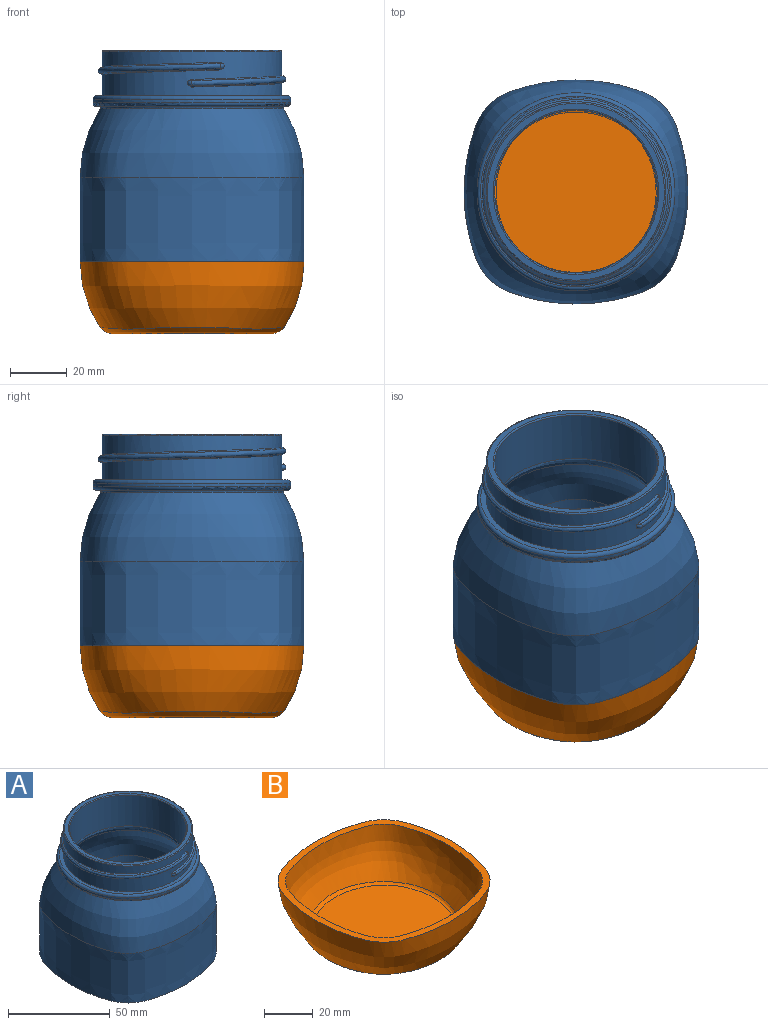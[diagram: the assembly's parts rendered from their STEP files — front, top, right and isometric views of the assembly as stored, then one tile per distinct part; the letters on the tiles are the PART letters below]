
ASSEMBLY  parts=2 mates=1
PART A: 27 faces, bbox 85.2x85.2x80.7 mm
  f0: cylinder r=31.75mm len=63.5mm, axis (0,0,-1), area 2519.4mm2, adj f1,f2,f5,f15,f19,f20,f22,f23
  f1: cone r=0.25mm half-angle=61.8deg, axis (-0.03,0,1), area 0.7mm2, adj f0,f19,f20
  f2: cone r=1.04mm half-angle=61.8deg, axis (0.03,0,-1), area 0.7mm2, adj f0,f19,f22
  f3: extruded ~78.99x78.99mm, area 7756.7mm2, adj f4,f26
  f4: bspline ~78.96x78.96mm, area 6303.1mm2, adj f3,f9
  f5: plane 67.31x67.31mm, normal (0,0,1), area 391.4mm2, adj f0,f18
  f6: plane 67.31x67.31mm, normal (0,0,-1), area 182.5mm2, adj f9,f17
  f7: cylinder r=34.92mm len=69.85mm, axis (0,0,-1), area 278.7mm2, adj f17,f18
  f8: plane 62.48x62.48mm, normal (0,0,1), area 385.9mm2, adj f15,f16
  f9: bspline ~65.42x65.42mm, area 228.7mm2, adj f4,f6
  f10: bspline ~59.42x59.41mm, area 630mm2, adj f12,f13
  f11: offset ~85.06x85.04mm, area 7156.8mm2, adj f12,f26
  f12: offset ~85.06x85.05mm, area 5387.2mm2, adj f10,f11
  f13: plane 59.36x59.35mm, normal (0,0,-1), area 137.5mm2, adj f10,f14
  f14: cylinder r=28.7mm len=57.4mm, axis (0,0,-1), area 3343.9mm2, adj f13,f16
  f15: torus R=31.24mm, axis (0,0,1), area 158.3mm2, adj f0,f8
  f16: torus R=29.21mm, axis (0,0,1), area 144.8mm2, adj f8,f14
  f17: torus R=33.65mm, axis (0,0,1), area 432mm2, adj f6,f7
  f18: torus R=33.65mm, axis (0,0,-1), area 432mm2, adj f5,f7
  f19: torus R=0.53mm, axis (-0.03,0,1), area 4.6mm2, adj f0,f1,f2,f21
  f20: bspline ~66.74x65.08mm, area 188.4mm2, adj f0,f1,f21,f23
  f21: bspline ~66.13x66.13mm, area 499.7mm2, adj f19,f20,f22,f25
  f22: bspline ~65.03x65.03mm, area 188.5mm2, adj f0,f2,f21,f24
  f23: cone r=1.04mm half-angle=61.8deg, axis (-0.03,-0.01,1), area 0.7mm2, adj f0,f20,f25
  f24: cone r=0.25mm half-angle=61.8deg, axis (0.03,0.01,-1), area 0.7mm2, adj f0,f22,f25
  f25: torus R=0.53mm, axis (0.03,0.01,-1), area 4.6mm2, adj f0,f21,f23,f24
  f26: plane 79.08x79.08mm, normal (0,0,-1), area 764.6mm2, adj f3,f11
PART B: 7 faces, bbox 85.1x85.1x31.5 mm
  f0: plane 56.52x56.52mm, normal (0,0,1), area 2541.8mm2, adj f1
  f1: bspline ~59.92x59.91mm, area 342.4mm2, adj f0,f2
  f2: offset ~85.06x85.06mm, area 5223.4mm2, adj f1,f3
  f3: plane 79.01x79.01mm, normal (0,0,1), area 765mm2, adj f2,f5
  f4: plane 56.52x56.52mm, normal (0,0,-1), area 2541.8mm2, adj f6
  f5: bspline ~78.96x78.96mm, area 6128.5mm2, adj f3,f6
  f6: bspline ~64.99x64.98mm, area 894mm2, adj f4,f5
PLACE A t=(-0.04,0.02,-40.33)mm
PLACE B at identity fixed
MATE fastened A.f26 <-> B.f3  axis (0,0,1) through (-22.26,-32.47,25.4)mm
